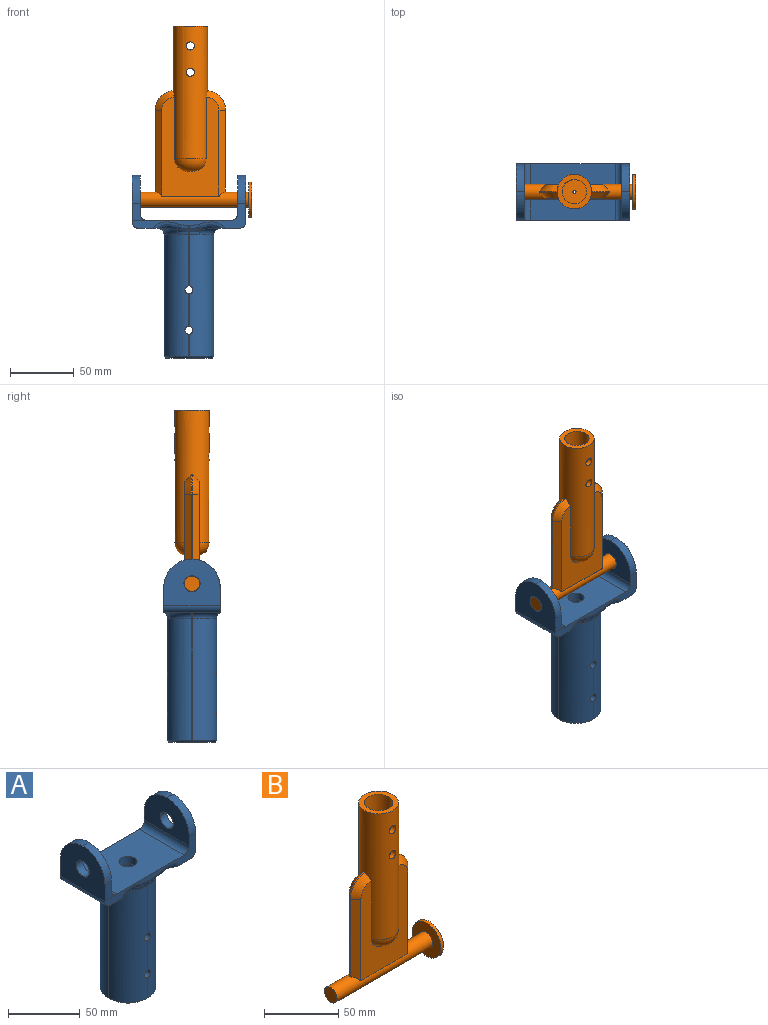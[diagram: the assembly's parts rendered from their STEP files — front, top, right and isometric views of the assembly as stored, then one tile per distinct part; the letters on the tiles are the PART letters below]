
ASSEMBLY  parts=2 mates=3
PART A: 72 faces, bbox 90.7x56.4x145 mm
  f0: plane 40.61x0.22mm, normal (0,1,0), area 8.7mm2, adj f2,f3,f37,f61
  f1: plane 40.61x0.22mm, normal (0,-1,0), area 8.7mm2, adj f4,f5,f26,f60
  f2: cylinder r=19.3mm len=95.84mm, axis (0,0,1), area 2860.4mm2, adj f0,f7,f12,f13,f33,f35,f53,f59
  f3: cylinder r=19.3mm len=95.84mm, axis (0,0,-1), area 2860.4mm2, adj f0,f7,f13,f14,f34,f36,f50,f59
  f4: cylinder r=19.3mm len=95.84mm, axis (0,0,1), area 2860.4mm2, adj f1,f8,f14,f15,f28,f30,f54,f58
  f5: cylinder r=19.3mm len=95.84mm, axis (0,0,-1), area 2860.4mm2, adj f1,f8,f12,f15,f27,f29,f57,f58
  f6: cylinder r=9.53mm len=101.6mm, axis (0,0,-1), area 5951.8mm2, adj f16,f48,f58,f59,f60,f61
  f7: plane 25.28x0.22mm, normal (0,1,0), area 5.4mm2, adj f2,f3,f59,f61
  f8: plane 25.28x0.22mm, normal (0,-1,0), area 5.4mm2, adj f4,f5,f58,f60
  f9: plane 45.77x23.4mm, normal (0,0,-1), area 762.4mm2, adj f10,f20,f30,f32,f34,f40,f62,f67
  f10: plane 82.84x19.77mm, normal (0,1,0), area 407.2mm2, adj f9,f11,f17,f19,f21,f25,f38,f39
  f11: plane 77.76x44.23mm, normal (0,0,1), area 2808.6mm2, adj f10,f19,f20,f24,f38,f39,f49
  f12: plane 95.25x0.22mm, normal (1,0,0), area 20.5mm2, adj f2,f5,f31,f55
  f13: plane 17.26x0.22mm, normal (0,1,0), area 3.7mm2, adj f2,f3,f51,f59
  f14: plane 95.25x0.22mm, normal (-1,0,0), area 20.5mm2, adj f3,f4,f32,f52
  f15: plane 17.26x0.22mm, normal (0,-1,0), area 3.7mm2, adj f4,f5,f56,f58
  f16: plane 36.28x36.28mm, normal (0,0,-1), area 752.3mm2, adj f6,f50,f51,f52,f53,f54,f55,f56
  f17: plane 45.79x23.4mm, normal (0,0,-1), area 762.4mm2, adj f10,f20,f21,f22,f29,f31,f33,f41
  f18: plane 44.25x36.6mm, normal (1,0,0), area 1283.4mm2, adj f20,f22,f23,f41,f44,f45,f47
  f19: plane 44.23x36.77mm, normal (-1,0,0), area 1285mm2, adj f10,f11,f20,f24,f40,f42,f43,f46
  f20: plane 89.19x19.59mm, normal (0,-1,0), area 435.4mm2, adj f9,f11,f17,f18,f19,f21,f39,f40
  f21: plane 44.25x41.68mm, normal (-1,0,0), area 1002.7mm2, adj f10,f17,f20,f22,f23,f39,f44,f45
  f22: plane 19.59x6.35mm, normal (0,1,0), area 118.8mm2, adj f17,f18,f21,f41,f44
  f23: plane 6.35x0.05mm, normal (0,0,1), area 0.3mm2, adj f18,f21,f44,f45
  f24: plane 13.41x11.43mm, normal (0,-1,0), area 90.7mm2, adj f11,f19,f25,f38,f43
  f25: plane 44.08x30.42mm, normal (1,0,0), area 1004.9mm2, adj f10,f24,f38,f42,f43,f46
  f26: cylinder r=5.08mm len=3.45mm, axis (1,0,0), area 0.8mm2, adj f1,f27,f28,f65
  f27: bspline ~13.63x5.43mm, area 36.9mm2, adj f5,f26,f29,f66
  f28: bspline ~13.63x5.43mm, area 36.9mm2, adj f4,f26,f30,f63
  f29: torus R=24.38mm, axis (0,0,1), area 177.4mm2, adj f5,f17,f27,f31,f64
  f30: torus R=24.38mm, axis (0,0,1), area 177.4mm2, adj f4,f9,f28,f32,f62
  f31: cylinder r=5.08mm len=5.08mm, axis (0,-1,0), area 1.7mm2, adj f12,f17,f29,f33
  f32: cylinder r=5.08mm len=5.08mm, axis (0,1,0), area 1.7mm2, adj f9,f14,f30,f34
  f33: torus R=24.38mm, axis (0,0,1), area 177.4mm2, adj f2,f17,f31,f35,f69
  f34: torus R=24.38mm, axis (0,0,1), area 177.4mm2, adj f3,f9,f32,f36,f67
  f35: bspline ~13.63x5.43mm, area 36.9mm2, adj f2,f33,f37,f71
  f36: bspline ~13.63x5.43mm, area 36.9mm2, adj f3,f34,f37,f68
  f37: cylinder r=5.08mm len=3.45mm, axis (1,0,0), area 0.8mm2, adj f0,f35,f36,f70
  f38: cylinder r=5.08mm len=44.08mm, axis (0,-1,0), area 351.8mm2, adj f10,f11,f24,f25
  f39: cylinder r=5.08mm len=44.23mm, axis (0,1,0), area 352.9mm2, adj f10,f11,f20,f21
  f40: cylinder r=5.08mm len=44.23mm, axis (0,-1,0), area 352.9mm2, adj f9,f10,f19,f20
  f41: cylinder r=5.08mm len=44.25mm, axis (0,1,0), area 353.1mm2, adj f17,f18,f20,f22
  f42: cylinder r=22.1mm len=22.1mm, axis (-1,0,0), area 220.1mm2, adj f10,f19,f25,f43
  f43: cylinder r=22.1mm len=22.1mm, axis (1,0,0), area 220.1mm2, adj f19,f24,f25,f42
  f44: cylinder r=22.1mm len=22.1mm, axis (-1,0,0), area 220.4mm2, adj f18,f21,f22,f23
  f45: cylinder r=22.1mm len=22.1mm, axis (-1,0,0), area 220.4mm2, adj f18,f20,f21,f23
  f46: cylinder r=6.35mm len=12.7mm, axis (-1,0,0), area 253.4mm2, adj f19,f25
  f47: cylinder r=6.35mm len=12.7mm, axis (-1,0,0), area 253.4mm2, adj f18,f21
  f48: plane 19.05x19.05mm, normal (0,0,-1), area 158.3mm2, adj f6,f49
  f49: cylinder r=6.35mm len=12.7mm, axis (0,0,-1), area 253.4mm2, adj f11,f48
  f50: cone r=18.03mm half-angle=45deg, axis (0,0,1), area 52.7mm2, adj f3,f16,f51,f52
  f51: plane 1.27x1.27mm, normal (0,0.71,-0.71), area 0.4mm2, adj f13,f16,f50,f53
  f52: plane 1.27x1.27mm, normal (-0.71,0,-0.71), area 0.4mm2, adj f14,f16,f50,f54
  f53: cone r=18.03mm half-angle=45deg, axis (0,0,1), area 52.7mm2, adj f2,f16,f51,f55
  f54: cone r=18.03mm half-angle=45deg, axis (0,0,1), area 52.7mm2, adj f4,f16,f52,f56
  f55: plane 1.27x1.27mm, normal (0.71,0,-0.71), area 0.4mm2, adj f12,f16,f53,f57
  f56: plane 1.27x1.27mm, normal (0,-0.71,-0.71), area 0.4mm2, adj f15,f16,f54,f57
  f57: cone r=18.03mm half-angle=45deg, axis (0,0,1), area 52.7mm2, adj f5,f16,f55,f56
  f58: cylinder r=3.17mm len=10.43mm, axis (0,-1,0), area 200.2mm2, adj f4,f5,f6,f8,f15
  f59: cylinder r=3.17mm len=10.43mm, axis (0,-1,0), area 200.2mm2, adj f2,f3,f6,f7,f13
  f60: cylinder r=3.17mm len=10.43mm, axis (0,-1,0), area 200.2mm2, adj f1,f4,f5,f6,f8
  f61: cylinder r=3.17mm len=10.43mm, axis (0,-1,0), area 200.2mm2, adj f0,f2,f3,f6,f7
  f62: bspline ~22.05x9.77mm, area 105.3mm2, adj f9,f20,f30,f63
  f63: bspline ~11.44x4.48mm, area 37.4mm2, adj f20,f28,f62,f65
  f64: bspline ~21.88x9.71mm, area 105.3mm2, adj f17,f20,f29,f66
  f65: cylinder r=5.08mm len=3.45mm, axis (1,0,0), area 0.8mm2, adj f20,f26,f63,f66
  f66: bspline ~11.59x4.51mm, area 37.4mm2, adj f20,f27,f64,f65
  f67: bspline ~21.88x9.71mm, area 105.3mm2, adj f9,f10,f34,f68
  f68: bspline ~11.59x4.51mm, area 37.4mm2, adj f10,f36,f67,f70
  f69: bspline ~22.05x9.77mm, area 105.3mm2, adj f10,f17,f33,f71
  f70: cylinder r=5.08mm len=3.45mm, axis (1,0,0), area 0.8mm2, adj f10,f37,f68,f71
  f71: bspline ~11.44x4.48mm, area 37.4mm2, adj f10,f35,f69,f70
PART B: 32 faces, bbox 94.8x28.3x150.7 mm
  f0: cylinder r=13.47mm len=104.14mm, axis (0,0,-1), area 7456mm2, adj f3,f4,f13,f14,f15,f16,f17,f20
  f1: cylinder r=9.53mm len=101.6mm, axis (0,0,1), area 5951.8mm2, adj f13,f19,f20,f21,f22,f23
  f2: cylinder r=6.01mm len=91.44mm, axis (-1,0,0), area 2789.3mm2, adj f5,f8,f9,f10,f11,f12,f18,f24
  f3: plane 77.53x44.88mm, normal (0,1,0), area 2052.9mm2, adj f0,f9,f15,f26,f27,f30,f31
  f4: plane 77.53x44.88mm, normal (0,-1,0), area 2052.9mm2, adj f0,f10,f14,f24,f25,f28,f29
  f5: plane 12.03x12.03mm, normal (-1,0,0), area 113.6mm2, adj f2
  f6: cylinder r=13.73mm len=27.45mm, axis (-1,0,0), area 219.1mm2, adj f7,f8
  f7: plane 27.45x27.45mm, normal (1,0,0), area 591.9mm2, adj f6
  f8: plane 27.45x27.45mm, normal (-1,0,0), area 478.2mm2, adj f2,f6
  f9: plane 45.36x0.25mm, normal (0,0,-1), area 11.2mm2, adj f2,f3,f26,f30
  f10: plane 45.36x0.25mm, normal (0,0,-1), area 11.2mm2, adj f2,f4,f24,f28
  f11: plane 64.16x0.98mm, normal (1,0,0), area 62.9mm2, adj f2,f16,f24,f26
  f12: plane 64.16x0.98mm, normal (-1,0,0), area 62.9mm2, adj f2,f17,f28,f30
  f13: plane 26.94x26.94mm, normal (0,0,1), area 285mm2, adj f0,f1
  f14: torus R=3.31mm, axis (0,0,1), area 294.3mm2, adj f0,f4
  f15: torus R=3.31mm, axis (0,0,1), area 294.3mm2, adj f0,f3
  f16: bspline ~15.2x14.15mm, area 22.7mm2, adj f0,f11,f25,f27
  f17: bspline ~15.2x14.15mm, area 22.7mm2, adj f0,f12,f29,f31
  f18: cylinder r=1.27mm len=40.56mm, axis (0,0,1), area 323.7mm2, adj f2,f19
  f19: plane 19.05x19.05mm, normal (0,0,1), area 280mm2, adj f1,f18
  f20: cylinder r=3.17mm len=6.35mm, axis (0,1,0), area 78.7mm2, adj f0,f1
  f21: cylinder r=3.17mm len=6.35mm, axis (0,1,0), area 78.7mm2, adj f0,f1
  f22: cylinder r=3.17mm len=6.35mm, axis (0,1,0), area 78.7mm2, adj f0,f1
  f23: cylinder r=3.17mm len=6.35mm, axis (0,1,0), area 78.7mm2, adj f0,f1
  f24: plane 68.19x5.91mm, normal (0.71,-0.71,0), area 468.9mm2, adj f2,f4,f10,f11,f25
  f25: bspline ~15.25x15.24mm, area 139.4mm2, adj f0,f4,f16,f24
  f26: plane 68.19x5.91mm, normal (0.71,0.71,0), area 468.9mm2, adj f2,f3,f9,f11,f27
  f27: bspline ~15.25x15.24mm, area 139.4mm2, adj f0,f3,f16,f26
  f28: plane 68.19x5.91mm, normal (-0.71,-0.71,0), area 468.9mm2, adj f2,f4,f10,f12,f29
  f29: bspline ~15.25x15.24mm, area 139.4mm2, adj f0,f4,f17,f28
  f30: plane 68.19x5.91mm, normal (-0.71,0.71,0), area 468.9mm2, adj f2,f3,f9,f12,f31
  f31: bspline ~15.25x15.24mm, area 139.4mm2, adj f0,f3,f17,f30
PLACE A t=(-151.39,57.07,-28.02)mm
PLACE B t=(-150.27,57.13,-28.12)mm
MATE pin_slot A.f46 <-> A.f19  axis (-1,0,0) through (-195.99,57.07,96.08)mm
MATE pin_slot B.f2 <-> A.f46  axis (-1,0,0) through (-195.99,57.13,96.08)mm
MATE pin_slot A.f42 <-> A.f46  axis (-1,0,0) through (-195.99,57.09,93.33)mm
